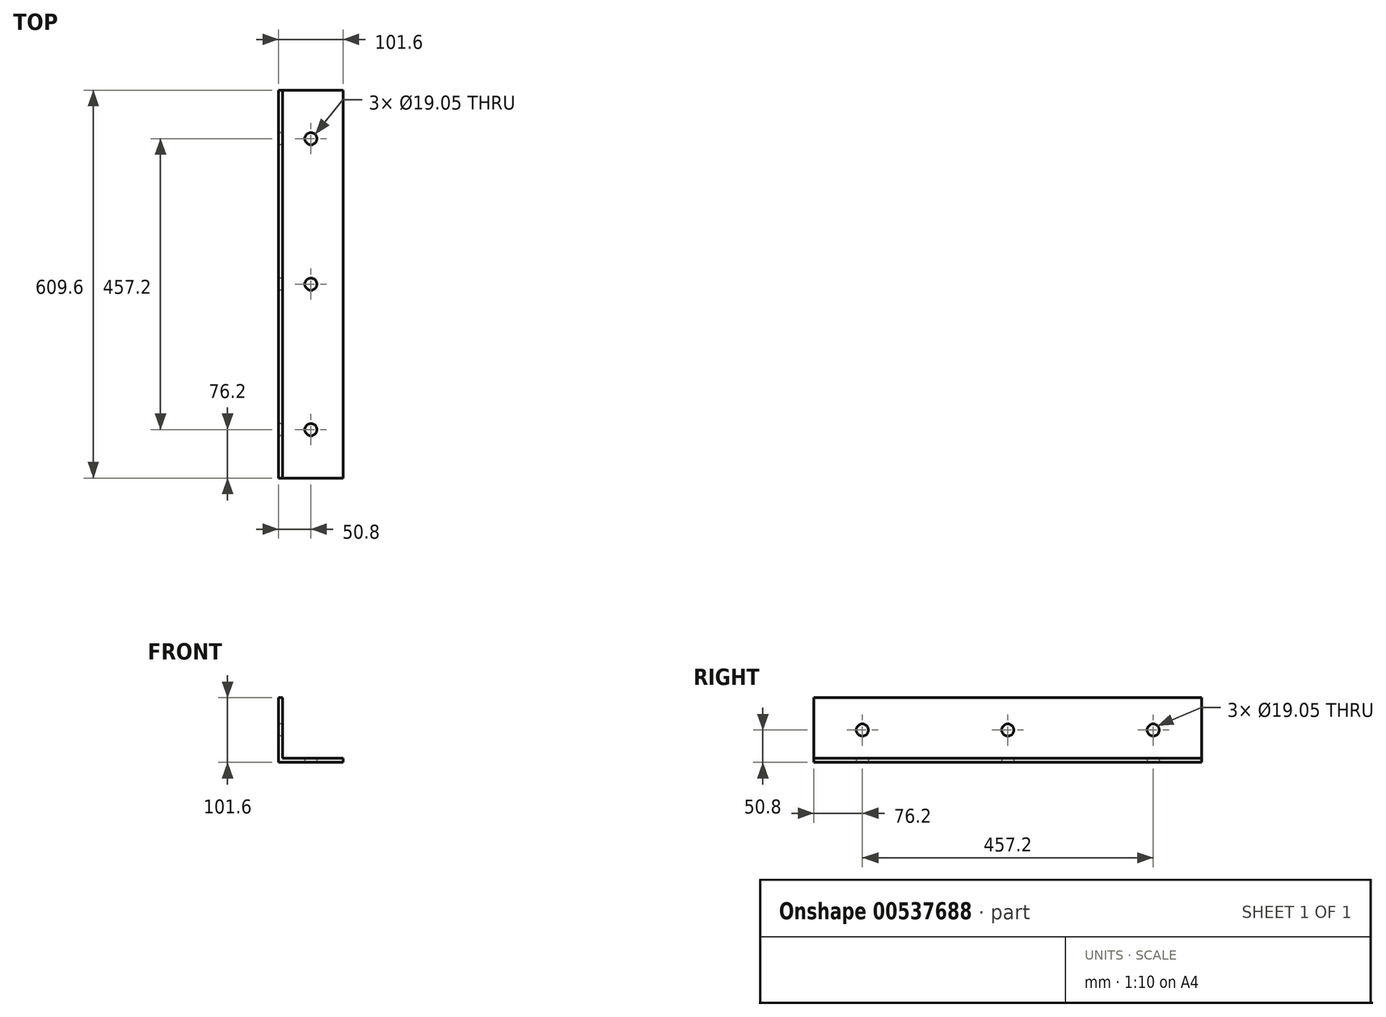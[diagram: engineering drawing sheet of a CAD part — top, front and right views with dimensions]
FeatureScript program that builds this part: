
annotation { "Feature Type Name" : "Feature", "Feature Type Description" : "" }
export const myFeature = defineFeature(function(context is Context, id is Id, definition is map)
    precondition{}
    {
        {
            var Q0;
            Q0=qCreatedBy(makeId("Front.planeOp"),FACE);
            var sketch = newSketch(context, id + "F0", { "sketchPlane" : qUnion([Q0])});
            skLineSegment(sketch, "E0", {"start": v(0, 0) * mm, "end": v(0, 101.6) * mm});
            skLineSegment(sketch, "E1", {"start": v(0, 101.6) * mm, "end": v(6.35, 101.6) * mm});
            skLineSegment(sketch, "E2", {"start": v(6.35, 101.6) * mm, "end": v(6.35, 6.35) * mm});
            skLineSegment(sketch, "E3", {"start": v(6.35, 6.35) * mm, "end": v(101.6, 6.35) * mm});
            skLineSegment(sketch, "E4", {"start": v(101.6, 6.35) * mm, "end": v(101.6, 0) * mm});
            skLineSegment(sketch, "E5", {"start": v(101.6, 0) * mm, "end": v(0, 0) * mm});
            skSolve(sketch);
        }
        {
            var Q0;
            Q0=makeQuery(id+"F0.imprint","IMPRINT",FACE,{"disambiguationData":[TD([[makeQuery(id+"F0.imprint","IMPRINT",EDGE,{"derivedFrom":sQuery(id+"F0.wireOp",EDGE,"E0")}),-1.0]])]});
            extrude(context, id + "F1", {"entities" : qUnion([Q0]), "oppositeDirection" : true, "depth" : 609.6 * mm, "offsetDistance" : 25.4 * mm});
        }
        {
            var Q0;
            Q0=makeQuery(id+"F1.opExtrude","SWEPT_FACE",FACE,{"disambiguationData":[OSD([sQuery(id+"F0.wireOp",EDGE,"E0")])]});
            var sketch = newSketch(context, id + "F2", { "sketchPlane" : qUnion([Q0])});
            skLineSegment(sketch, "E6", {"start": v(-620.26, 50.8) * mm, "end": v(63.4, 50.8) * mm, "construction": true});
            skLineSegment(sketch, "E7.0", {"start": v(-609.6, 101.6) * mm, "end": v(0, 101.6) * mm, "construction": true});
            skLineSegment(sketch, "E8.0", {"start": v(-609.6, 0) * mm, "end": v(-609.6, 101.6) * mm, "construction": true});
            skCircle(sketch, "E9", {"center": v(-533.4, 50.8) * mm, "radius": 9.53 * mm});
            skCircle(sketch, "E10", {"center": v(-304.8, 50.8) * mm, "radius": 9.53 * mm});
            skCircle(sketch, "E11", {"center": v(-76.2, 50.8) * mm, "radius": 9.53 * mm});
            skSolve(sketch);
        }
        {
            var Q0;
            Q0 = qSketchRegion(id + "F2", true);
            extrude(context, id + "F3", {"entities" : qUnion([Q0]), "operationType" : NewBodyOperationType.REMOVE, "oppositeDirection" : true, "depth" : 25.4 * mm, "offsetDistance" : 25.4 * mm});
        }
        {
            var Q0;
            Q0=makeQuery(id+"F1.opExtrude","SWEPT_FACE",FACE,{"disambiguationData":[OSD([sQuery(id+"F0.wireOp",EDGE,"E5")])]});
            var sketch = newSketch(context, id + "F4", { "sketchPlane" : qUnion([Q0])});
            skLineSegment(sketch, "E12.0", {"start": v(101.6, -609.6) * mm, "end": v(101.6, 0) * mm, "construction": true});
            skLineSegment(sketch, "E12.1", {"start": v(101.6, -609.6) * mm, "end": v(0, -609.6) * mm, "construction": true});
            skLineSegment(sketch, "E13", {"start": v(50.8, 37.17) * mm, "end": v(50.8, -640.06) * mm, "construction": true});
            skCircle(sketch, "E14", {"center": v(50.8, -533.4) * mm, "radius": 9.53 * mm});
            skCircle(sketch, "E15", {"center": v(50.8, -304.8) * mm, "radius": 9.53 * mm});
            skCircle(sketch, "E16", {"center": v(50.8, -76.2) * mm, "radius": 9.53 * mm});
            skSolve(sketch);
        }
        {
            var Q0;
            Q0 = qSketchRegion(id + "F4", true);
            extrude(context, id + "F5", {"entities" : qUnion([Q0]), "operationType" : NewBodyOperationType.REMOVE, "oppositeDirection" : true, "depth" : 25.4 * mm, "offsetDistance" : 25.4 * mm});
        }
    });
